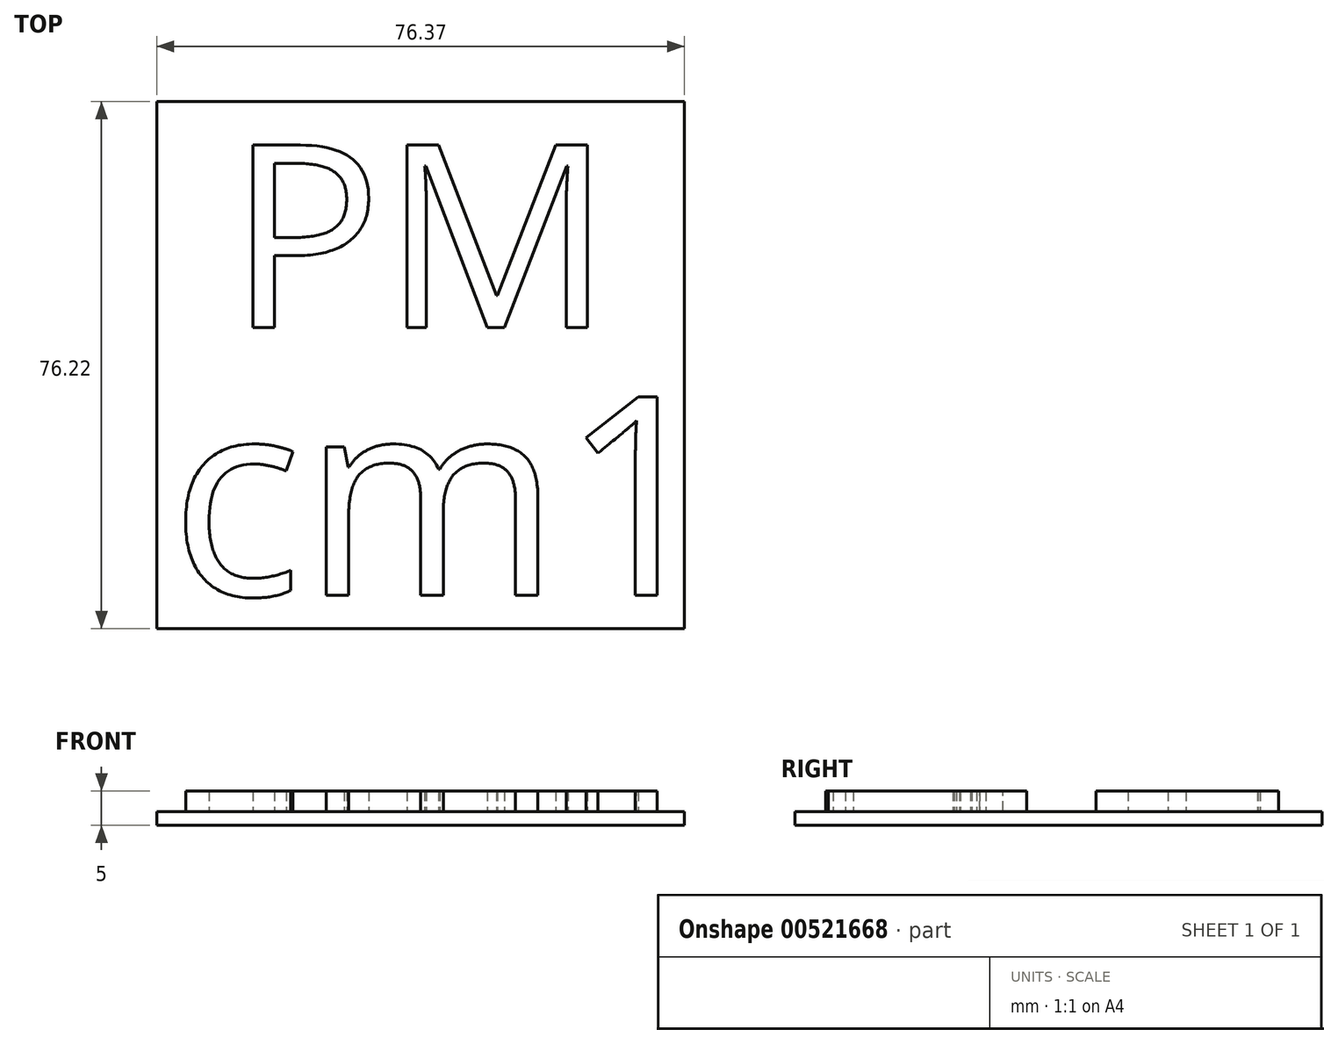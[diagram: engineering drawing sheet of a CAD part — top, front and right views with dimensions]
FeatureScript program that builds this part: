
annotation { "Feature Type Name" : "Feature", "Feature Type Description" : "" }
export const myFeature = defineFeature(function(context is Context, id is Id, definition is map)
    precondition{}
    {
        {
            var Q0;
            Q0=qCreatedBy(makeId("Top.planeOp"),FACE);
            var sketch = newSketch(context, id + "F0", { "sketchPlane" : qUnion([Q0])});
            skLineSegment(sketch, "E0.bottom", {"start": v(-76.37, 76.22) * mm, "end": v(0, 76.22) * mm});
            skLineSegment(sketch, "E0.top", {"start": v(-76.37, 0) * mm, "end": v(0, 0) * mm});
            skLineSegment(sketch, "E0.left", {"start": v(-76.37, 76.22) * mm, "end": v(-76.37, 0) * mm});
            skLineSegment(sketch, "E0.right", {"start": v(0, 76.22) * mm, "end": v(0, 0) * mm});
            skSolve(sketch);
        }
        {
            var Q0;
            Q0=makeQuery(id+"F0.imprint","IMPRINT",FACE,{"disambiguationData":[TD([[makeQuery(id+"F0.imprint","IMPRINT",EDGE,{"derivedFrom":sQuery(id+"F0.wireOp",EDGE,"E0.bottom")}),-1.0]])]});
            extrude(context, id + "F1", {"entities" : qUnion([Q0]), "depth" : 2 * mm, "offsetDistance" : 25 * mm});
        }
        {
            var Q0;
            Q0=makeQuery(id+"F1.opExtrude","CAP_FACE",FACE,{"disambiguationData":[OSD([sQuery(id+"F0.wireOp",EDGE,"E0.bottom"),sQuery(id+"F0.wireOp",EDGE,"E0.top"),sQuery(id+"F0.wireOp",EDGE,"E0.left"),sQuery(id+"F0.wireOp",EDGE,"E0.right")])],"isStart":false});
            var sketch = newSketch(context, id + "F2", { "sketchPlane" : qUnion([Q0])});
            skText(sketch, "E1", { "text": "PM", "fontName": "OpenSans-Regular.ttf"});
            skText(sketch, "E2", { "text": "cm1", "fontName": "OpenSans-Regular.ttf"});
            const initialGuessF2  = {"E1": [-0.06605, 0.04356, 1, 0, 0.0266], "E2": [-0.07444, 0.0048, 1, 0, 0.02892]};
            skSetInitialGuess(sketch, initialGuessF2);
            skSolve(sketch);
        }
        {
            var Q0;
            Q0 = qSketchRegion(id + "F2", true);
            extrude(context, id + "F3", {"entities" : qUnion([Q0]), "operationType" : NewBodyOperationType.ADD, "depth" : 3 * mm, "offsetDistance" : 25 * mm});
        }
    });
